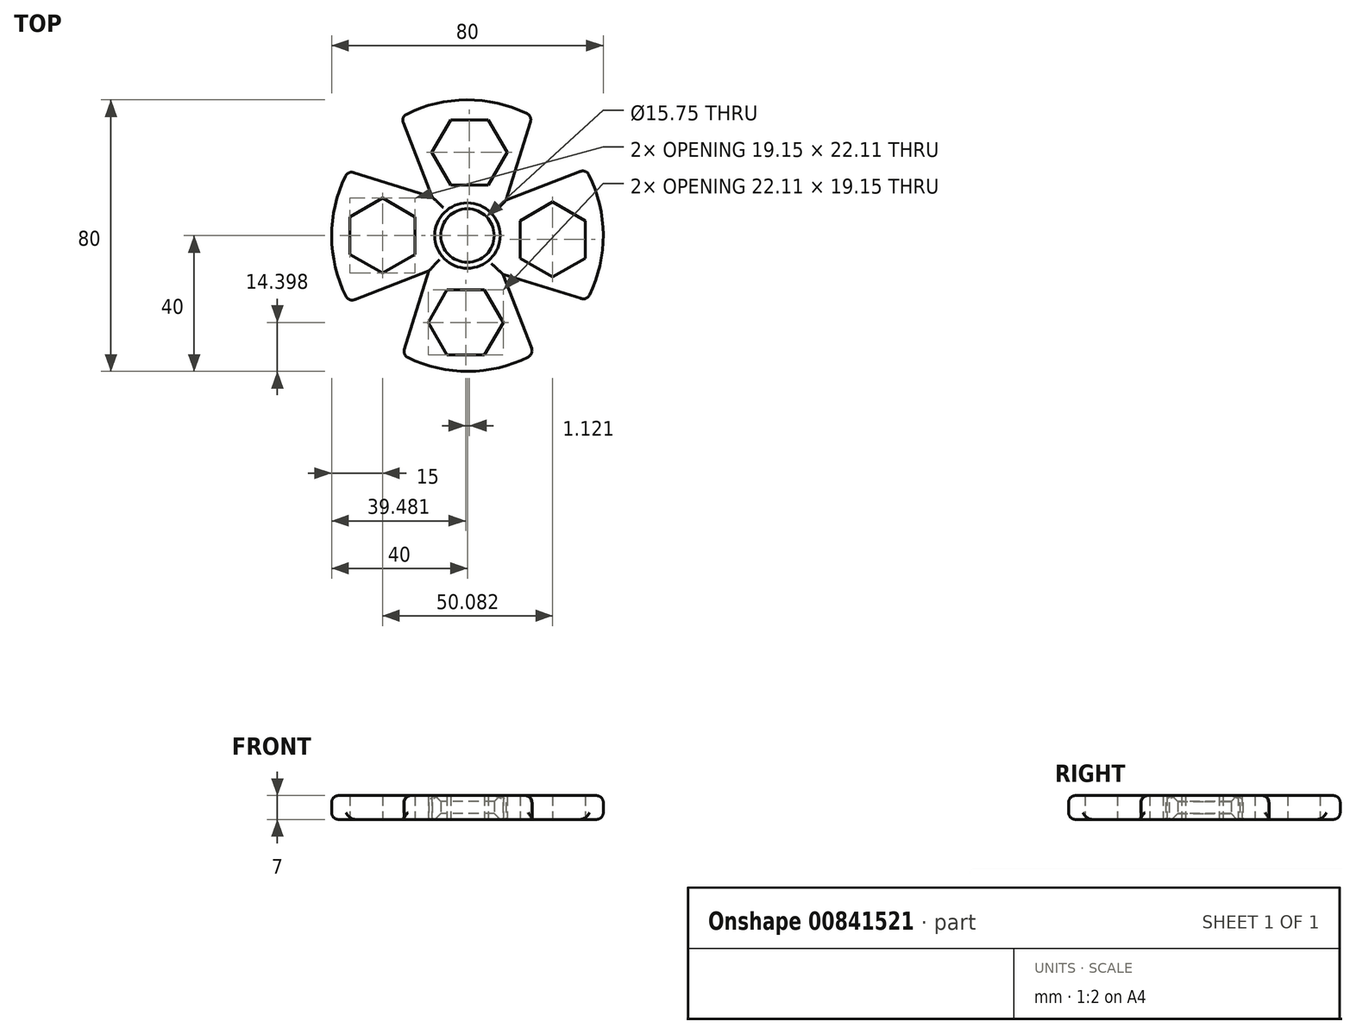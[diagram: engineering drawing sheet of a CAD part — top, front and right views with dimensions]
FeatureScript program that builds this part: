
annotation { "Feature Type Name" : "Feature", "Feature Type Description" : "" }
export const myFeature = defineFeature(function(context is Context, id is Id, definition is map)
    precondition{}
    {
        {
            var Q0;
            Q0=qCreatedBy(makeId("Top.planeOp"),FACE);
            var sketch = newSketch(context, id + "F0", { "sketchPlane" : qUnion([Q0])});
            skCircle(sketch, "E0", {"center": v(0, 0) * mm, "radius": 7.88 * mm});
            skCircle(sketch, "E1", {"center": v(0, 0) * mm, "radius": 40 * mm});
            skSolve(sketch);
        }
        {
            var Q0;
            Q0=makeQuery(id+"F0.imprint","IMPRINT",FACE,{"disambiguationData":[TD([[makeQuery(id+"F0.imprint","IMPRINT",EDGE,{"derivedFrom":sQuery(id+"F0.wireOp",EDGE,"E0")}),-1.0]])]});
            extrude(context, id + "F1", {"entities" : qUnion([Q0]), "depth" : 7 * mm, "offsetDistance" : 25 * mm});
        }
        {
            var Q0;
            Q0=qCreatedBy(makeId("Top.planeOp"),FACE);
            var sketch = newSketch(context, id + "F2", { "sketchPlane" : qUnion([Q0])});
            skCircle(sketch, "E2.cCircle", {"center": v(-25, 0) * mm, "radius": 9.58 * mm, "construction": true});
            skLineSegment(sketch, "E2.0", {"start": v(-15.42, -5.53) * mm, "end": v(-25, -11.06) * mm});
            skLineSegment(sketch, "E2.1", {"start": v(-25, -11.06) * mm, "end": v(-34.57, -5.53) * mm});
            skLineSegment(sketch, "E2.2", {"start": v(-34.57, -5.53) * mm, "end": v(-34.58, 5.53) * mm});
            skLineSegment(sketch, "E2.3", {"start": v(-34.58, 5.53) * mm, "end": v(-25, 11.06) * mm});
            skLineSegment(sketch, "E2.4", {"start": v(-25, 11.06) * mm, "end": v(-15.43, 5.53) * mm});
            skLineSegment(sketch, "E2.5", {"start": v(-15.43, 5.53) * mm, "end": v(-15.42, -5.53) * mm});
            skPoint(sketch, "E2.0.midPoint", {"position": v(-20.21, -8.3) * mm});
            skLineSegment(sketch, "E3.1.0", {"start": v(-11.58, -25.6) * mm, "end": v(-6.05, -16.03) * mm});
            skLineSegment(sketch, "E3.1.1", {"start": v(-6.05, -35.18) * mm, "end": v(-11.58, -25.6) * mm});
            skLineSegment(sketch, "E3.1.2", {"start": v(5, -35.18) * mm, "end": v(-6.05, -35.18) * mm});
            skLineSegment(sketch, "E3.1.3", {"start": v(10.54, -25.6) * mm, "end": v(5, -35.18) * mm});
            skLineSegment(sketch, "E3.1.4", {"start": v(5, -16.03) * mm, "end": v(10.54, -25.6) * mm});
            skLineSegment(sketch, "E3.1.5", {"start": v(-6.05, -16.03) * mm, "end": v(5, -16.03) * mm});
            skLineSegment(sketch, "E3.2.0", {"start": v(25.08, -12.18) * mm, "end": v(15.5, -6.65) * mm});
            skLineSegment(sketch, "E3.2.1", {"start": v(34.66, -6.65) * mm, "end": v(25.08, -12.18) * mm});
            skLineSegment(sketch, "E3.2.2", {"start": v(34.66, 4.4) * mm, "end": v(34.66, -6.65) * mm});
            skLineSegment(sketch, "E3.2.3", {"start": v(25.08, 9.94) * mm, "end": v(34.66, 4.4) * mm});
            skLineSegment(sketch, "E3.2.4", {"start": v(15.5, 4.4) * mm, "end": v(25.08, 9.94) * mm});
            skLineSegment(sketch, "E3.2.5", {"start": v(15.5, -6.65) * mm, "end": v(15.5, 4.4) * mm});
            skLineSegment(sketch, "E3.3.0", {"start": v(11.66, 24.48) * mm, "end": v(6.13, 14.9) * mm});
            skLineSegment(sketch, "E3.3.1", {"start": v(6.13, 34.06) * mm, "end": v(11.66, 24.48) * mm});
            skLineSegment(sketch, "E3.3.2", {"start": v(-4.93, 34.06) * mm, "end": v(6.13, 34.06) * mm});
            skLineSegment(sketch, "E3.3.3", {"start": v(-10.45, 24.48) * mm, "end": v(-4.93, 34.06) * mm});
            skLineSegment(sketch, "E3.3.4", {"start": v(-4.93, 14.9) * mm, "end": v(-10.45, 24.48) * mm});
            skLineSegment(sketch, "E3.3.5", {"start": v(6.13, 14.9) * mm, "end": v(-4.93, 14.9) * mm});
            skPoint(sketch, "E3.center", {"position": v(0.04, -0.56) * mm});
            skSolve(sketch);
        }
        {
            var Q0;
            Q0=qSketchRegion(id+"F2",true);
            extrude(context, id + "F3", {"entities" : qUnion([Q0]), "operationType" : NewBodyOperationType.REMOVE, "endBound" : BoundingType.THROUGH_ALL, "depth" : 25 * mm, "offsetDistance" : 25 * mm});
        }
        {
            var Q0;
            Q0=qCreatedBy(makeId("Top.planeOp"),FACE);
            var sketch = newSketch(context, id + "F4", { "sketchPlane" : qUnion([Q0])});
            skLineSegment(sketch, "E4", {"start": v(-19.58, 35.02) * mm, "end": v(-10.44, 11.39) * mm});
            skLineSegment(sketch, "E5", {"start": v(-10.44, 11.39) * mm, "end": v(-58.22, 26.22) * mm});
            skLineSegment(sketch, "E6", {"start": v(-58.22, 26.22) * mm, "end": v(-19.58, 35.02) * mm});
            skLineSegment(sketch, "E7.1.0", {"start": v(-26.22, -58.22) * mm, "end": v(-35.02, -19.58) * mm});
            skLineSegment(sketch, "E7.1.1", {"start": v(-11.39, -10.44) * mm, "end": v(-26.22, -58.22) * mm});
            skLineSegment(sketch, "E7.1.2", {"start": v(-35.02, -19.58) * mm, "end": v(-11.39, -10.44) * mm});
            skLineSegment(sketch, "E7.2.0", {"start": v(58.22, -26.22) * mm, "end": v(19.58, -35.02) * mm});
            skLineSegment(sketch, "E7.2.1", {"start": v(10.44, -11.39) * mm, "end": v(58.22, -26.22) * mm});
            skLineSegment(sketch, "E7.2.2", {"start": v(19.58, -35.02) * mm, "end": v(10.44, -11.39) * mm});
            skLineSegment(sketch, "E7.3.0", {"start": v(26.22, 58.22) * mm, "end": v(35.02, 19.58) * mm});
            skLineSegment(sketch, "E7.3.1", {"start": v(11.39, 10.44) * mm, "end": v(26.22, 58.22) * mm});
            skLineSegment(sketch, "E7.3.2", {"start": v(35.02, 19.58) * mm, "end": v(11.39, 10.44) * mm});
            skPoint(sketch, "E7.center", {"position": v(0, 0) * mm});
            skSolve(sketch);
        }
        {
            var Q0;
            Q0=makeQuery(id+"F4.imprint","IMPRINT",FACE,{"disambiguationData":[TD([[makeQuery(id+"F4.imprint","IMPRINT",EDGE,{"derivedFrom":sQuery(id+"F4.wireOp",EDGE,"E4")}),-1.0]])]});
            var Q1;
            Q1=makeQuery(id+"F4.imprint","IMPRINT",FACE,{"disambiguationData":[TD([[makeQuery(id+"F4.imprint","IMPRINT",EDGE,{"derivedFrom":sQuery(id+"F4.wireOp",EDGE,"E7.1.0")}),-1.0]])]});
            var Q2;
            Q2=makeQuery(id+"F4.imprint","IMPRINT",FACE,{"disambiguationData":[TD([[makeQuery(id+"F4.imprint","IMPRINT",EDGE,{"derivedFrom":sQuery(id+"F4.wireOp",EDGE,"E7.2.0")}),-1.0]])]});
            var Q3;
            Q3=makeQuery(id+"F4.imprint","IMPRINT",FACE,{"disambiguationData":[TD([[makeQuery(id+"F4.imprint","IMPRINT",EDGE,{"derivedFrom":sQuery(id+"F4.wireOp",EDGE,"E7.3.0")}),-1.0]])]});
            extrude(context, id + "F5", {"entities" : qUnion([Q0, Q1, Q2, Q3]), "operationType" : NewBodyOperationType.REMOVE, "endBound" : BoundingType.THROUGH_ALL, "depth" : 25 * mm, "offsetDistance" : 25 * mm});
        }
        {
            var Q0;
            Q0=makeQuery(id+"F5.boolean.opBoolean","INTERSECT",EDGE,{"derivedFrom":[makeQuery(id+"F1.opExtrude","CAP_FACE",FACE,{"disambiguationData":[OSD([sQuery(id+"F0.wireOp",EDGE,"E0"),sQuery(id+"F0.wireOp",EDGE,"E1")])],"isStart":false}),makeQuery(id+"F5.opExtrude","SWEPT_FACE",FACE,{"disambiguationData":[OSD([sQuery(id+"F4.wireOp",EDGE,"E5")])]})]});
            var Q1;
            {var subQ0=sQuery(id+"F0.wireOp",EDGE,"E1");Q1=makeQuery(id+"F5.boolean.opBoolean","SPLIT",EDGE,{"disambiguationData":[TD([makeQuery(id+"F5.opExtrude","SWEPT_FACE",FACE,{"disambiguationData":[OSD([sQuery(id+"F4.wireOp",EDGE,"E5")])]})])],"derivedFrom":makeQuery(id+"F1.opExtrude","CAP_EDGE",EDGE,{"disambiguationData":[OSD([subQ0])],"isStart":false})});}
            var Q2;
            Q2=makeQuery(id+"F5.boolean.opBoolean","INTERSECT",EDGE,{"derivedFrom":[makeQuery(id+"F1.opExtrude","CAP_FACE",FACE,{"disambiguationData":[OSD([sQuery(id+"F0.wireOp",EDGE,"E0"),sQuery(id+"F0.wireOp",EDGE,"E1")])],"isStart":false}),makeQuery(id+"F5.opExtrude","SWEPT_FACE",FACE,{"disambiguationData":[OSD([sQuery(id+"F4.wireOp",EDGE,"E7.1.2")])]})]});
            var Q3;
            Q3=makeQuery(id+"F5.boolean.opBoolean","INTERSECT",EDGE,{"derivedFrom":[makeQuery(id+"F1.opExtrude","CAP_FACE",FACE,{"disambiguationData":[OSD([sQuery(id+"F0.wireOp",EDGE,"E0"),sQuery(id+"F0.wireOp",EDGE,"E1")])],"isStart":false}),makeQuery(id+"F5.opExtrude","SWEPT_FACE",FACE,{"disambiguationData":[OSD([sQuery(id+"F4.wireOp",EDGE,"E7.1.1")])]})]});
            var Q4;
            Q4=makeQuery(id+"F5.boolean.opBoolean","INTERSECT",EDGE,{"derivedFrom":[makeQuery(id+"F1.opExtrude","CAP_FACE",FACE,{"disambiguationData":[OSD([sQuery(id+"F0.wireOp",EDGE,"E0"),sQuery(id+"F0.wireOp",EDGE,"E1")])],"isStart":false}),makeQuery(id+"F5.opExtrude","SWEPT_FACE",FACE,{"disambiguationData":[OSD([sQuery(id+"F4.wireOp",EDGE,"E7.2.2")])]})]});
            var Q5;
            Q5=makeQuery(id+"F5.boolean.opBoolean","INTERSECT",EDGE,{"derivedFrom":[makeQuery(id+"F1.opExtrude","CAP_FACE",FACE,{"disambiguationData":[OSD([sQuery(id+"F0.wireOp",EDGE,"E0"),sQuery(id+"F0.wireOp",EDGE,"E1")])],"isStart":false}),makeQuery(id+"F5.opExtrude","SWEPT_FACE",FACE,{"disambiguationData":[OSD([sQuery(id+"F4.wireOp",EDGE,"E7.2.1")])]})]});
            var Q6;
            Q6=makeQuery(id+"F5.boolean.opBoolean","INTERSECT",EDGE,{"derivedFrom":[makeQuery(id+"F1.opExtrude","CAP_FACE",FACE,{"disambiguationData":[OSD([sQuery(id+"F0.wireOp",EDGE,"E0"),sQuery(id+"F0.wireOp",EDGE,"E1")])],"isStart":false}),makeQuery(id+"F5.opExtrude","SWEPT_FACE",FACE,{"disambiguationData":[OSD([sQuery(id+"F4.wireOp",EDGE,"E7.3.2")])]})]});
            var Q7;
            {var subQ0=sQuery(id+"F0.wireOp",EDGE,"E1");Q7=makeQuery(id+"F5.boolean.opBoolean","SPLIT",EDGE,{"disambiguationData":[TD([makeQuery(id+"F5.opExtrude","SWEPT_FACE",FACE,{"disambiguationData":[OSD([sQuery(id+"F4.wireOp",EDGE,"E7.2.1")])]})])],"derivedFrom":makeQuery(id+"F1.opExtrude","CAP_EDGE",EDGE,{"disambiguationData":[OSD([subQ0])],"isStart":false})});}
            var Q8;
            Q8=makeQuery(id+"F5.boolean.opBoolean","INTERSECT",EDGE,{"derivedFrom":[makeQuery(id+"F1.opExtrude","CAP_FACE",FACE,{"disambiguationData":[OSD([sQuery(id+"F0.wireOp",EDGE,"E0"),sQuery(id+"F0.wireOp",EDGE,"E1")])],"isStart":false}),makeQuery(id+"F5.opExtrude","SWEPT_FACE",FACE,{"disambiguationData":[OSD([sQuery(id+"F4.wireOp",EDGE,"E7.3.1")])]})]});
            var Q9;
            {var subQ0=sQuery(id+"F0.wireOp",EDGE,"E1");Q9=makeQuery(id+"F5.boolean.opBoolean","SPLIT",EDGE,{"disambiguationData":[TD([makeQuery(id+"F5.opExtrude","SWEPT_FACE",FACE,{"disambiguationData":[OSD([sQuery(id+"F4.wireOp",EDGE,"E4")])]})])],"derivedFrom":makeQuery(id+"F1.opExtrude","CAP_EDGE",EDGE,{"disambiguationData":[OSD([subQ0])],"isStart":false})});}
            var Q10;
            Q10=makeQuery(id+"F5.boolean.opBoolean","INTERSECT",EDGE,{"derivedFrom":[makeQuery(id+"F1.opExtrude","CAP_FACE",FACE,{"disambiguationData":[OSD([sQuery(id+"F0.wireOp",EDGE,"E0"),sQuery(id+"F0.wireOp",EDGE,"E1")])],"isStart":false}),makeQuery(id+"F5.opExtrude","SWEPT_FACE",FACE,{"disambiguationData":[OSD([sQuery(id+"F4.wireOp",EDGE,"E4")])]})]});
            var Q11;
            {var subQ0=sQuery(id+"F0.wireOp",EDGE,"E1");Q11=makeQuery(id+"F5.boolean.opBoolean","SPLIT",EDGE,{"disambiguationData":[TD([makeQuery(id+"F5.opExtrude","SWEPT_FACE",FACE,{"disambiguationData":[OSD([sQuery(id+"F4.wireOp",EDGE,"E5")])]})])],"derivedFrom":makeQuery(id+"F1.opExtrude","CAP_EDGE",EDGE,{"disambiguationData":[OSD([subQ0])],"isStart":true})});}
            var Q12;
            Q12=makeQuery(id+"F5.boolean.opBoolean","COPY",EDGE,{"derivedFrom":makeQuery(id+"F5.opExtrude","CAP_EDGE",EDGE,{"disambiguationData":[OSD([sQuery(id+"F4.wireOp",EDGE,"E5")])],"isStart":true})});
            var Q13;
            Q13=makeQuery(id+"F5.boolean.opBoolean","COPY",EDGE,{"derivedFrom":makeQuery(id+"F5.opExtrude","CAP_EDGE",EDGE,{"disambiguationData":[OSD([sQuery(id+"F4.wireOp",EDGE,"E4")])],"isStart":true})});
            var Q14;
            {var subQ0=sQuery(id+"F0.wireOp",EDGE,"E1");Q14=makeQuery(id+"F5.boolean.opBoolean","SPLIT",EDGE,{"disambiguationData":[TD([makeQuery(id+"F5.opExtrude","SWEPT_FACE",FACE,{"disambiguationData":[OSD([sQuery(id+"F4.wireOp",EDGE,"E4")])]})])],"derivedFrom":makeQuery(id+"F1.opExtrude","CAP_EDGE",EDGE,{"disambiguationData":[OSD([subQ0])],"isStart":true})});}
            var Q15;
            Q15=makeQuery(id+"F5.boolean.opBoolean","COPY",EDGE,{"derivedFrom":makeQuery(id+"F5.opExtrude","CAP_EDGE",EDGE,{"disambiguationData":[OSD([sQuery(id+"F4.wireOp",EDGE,"E7.3.1")])],"isStart":true})});
            var Q16;
            Q16=makeQuery(id+"F5.boolean.opBoolean","COPY",EDGE,{"derivedFrom":makeQuery(id+"F5.opExtrude","CAP_EDGE",EDGE,{"disambiguationData":[OSD([sQuery(id+"F4.wireOp",EDGE,"E7.3.2")])],"isStart":true})});
            var Q17;
            {var subQ0=sQuery(id+"F0.wireOp",EDGE,"E1");Q17=makeQuery(id+"F5.boolean.opBoolean","SPLIT",EDGE,{"disambiguationData":[TD([makeQuery(id+"F5.opExtrude","SWEPT_FACE",FACE,{"disambiguationData":[OSD([sQuery(id+"F4.wireOp",EDGE,"E7.2.1")])]})])],"derivedFrom":makeQuery(id+"F1.opExtrude","CAP_EDGE",EDGE,{"disambiguationData":[OSD([subQ0])],"isStart":true})});}
            var Q18;
            Q18=makeQuery(id+"F5.boolean.opBoolean","COPY",EDGE,{"derivedFrom":makeQuery(id+"F5.opExtrude","CAP_EDGE",EDGE,{"disambiguationData":[OSD([sQuery(id+"F4.wireOp",EDGE,"E7.2.1")])],"isStart":true})});
            var Q19;
            Q19=makeQuery(id+"F5.boolean.opBoolean","COPY",EDGE,{"derivedFrom":makeQuery(id+"F5.opExtrude","CAP_EDGE",EDGE,{"disambiguationData":[OSD([sQuery(id+"F4.wireOp",EDGE,"E7.2.2")])],"isStart":true})});
            var Q20;
            {var subQ0=sQuery(id+"F0.wireOp",EDGE,"E1");Q20=makeQuery(id+"F5.boolean.opBoolean","SPLIT",EDGE,{"disambiguationData":[TD([makeQuery(id+"F5.opExtrude","SWEPT_FACE",FACE,{"disambiguationData":[OSD([sQuery(id+"F4.wireOp",EDGE,"E7.1.1")])]})])],"derivedFrom":makeQuery(id+"F1.opExtrude","CAP_EDGE",EDGE,{"disambiguationData":[OSD([subQ0])],"isStart":true})});}
            var Q21;
            Q21=makeQuery(id+"F5.boolean.opBoolean","COPY",EDGE,{"derivedFrom":makeQuery(id+"F5.opExtrude","CAP_EDGE",EDGE,{"disambiguationData":[OSD([sQuery(id+"F4.wireOp",EDGE,"E7.1.1")])],"isStart":true})});
            var Q22;
            Q22=makeQuery(id+"F5.boolean.opBoolean","COPY",EDGE,{"derivedFrom":makeQuery(id+"F5.opExtrude","CAP_EDGE",EDGE,{"disambiguationData":[OSD([sQuery(id+"F4.wireOp",EDGE,"E7.1.2")])],"isStart":true})});
            var Q23;
            {var subQ0=sQuery(id+"F0.wireOp",EDGE,"E1");Q23=makeQuery(id+"F5.boolean.opBoolean","SPLIT",EDGE,{"disambiguationData":[TD([makeQuery(id+"F5.opExtrude","SWEPT_FACE",FACE,{"disambiguationData":[OSD([sQuery(id+"F4.wireOp",EDGE,"E7.1.1")])]})])],"derivedFrom":makeQuery(id+"F1.opExtrude","CAP_EDGE",EDGE,{"disambiguationData":[OSD([subQ0])],"isStart":false})});}
            var Q24;
            Q24=makeQuery(id+"F5.boolean.opBoolean","INTERSECT",EDGE,{"derivedFrom":[makeQuery(id+"F1.opExtrude","SWEPT_FACE",FACE,{"disambiguationData":[OSD([sQuery(id+"F0.wireOp",EDGE,"E1")])]}),makeQuery(id+"F5.opExtrude","SWEPT_FACE",FACE,{"disambiguationData":[OSD([sQuery(id+"F4.wireOp",EDGE,"E7.2.2")])]})]});
            var Q25;
            Q25=makeQuery(id+"F5.boolean.opBoolean","INTERSECT",EDGE,{"derivedFrom":[makeQuery(id+"F1.opExtrude","SWEPT_FACE",FACE,{"disambiguationData":[OSD([sQuery(id+"F0.wireOp",EDGE,"E1")])]}),makeQuery(id+"F5.opExtrude","SWEPT_FACE",FACE,{"disambiguationData":[OSD([sQuery(id+"F4.wireOp",EDGE,"E7.1.1")])]})]});
            var Q26;
            Q26=makeQuery(id+"F5.boolean.opBoolean","INTERSECT",EDGE,{"derivedFrom":[makeQuery(id+"F1.opExtrude","SWEPT_FACE",FACE,{"disambiguationData":[OSD([sQuery(id+"F0.wireOp",EDGE,"E1")])]}),makeQuery(id+"F5.opExtrude","SWEPT_FACE",FACE,{"disambiguationData":[OSD([sQuery(id+"F4.wireOp",EDGE,"E7.1.2")])]})]});
            var Q27;
            Q27=makeQuery(id+"F5.boolean.opBoolean","INTERSECT",EDGE,{"derivedFrom":[makeQuery(id+"F1.opExtrude","SWEPT_FACE",FACE,{"disambiguationData":[OSD([sQuery(id+"F0.wireOp",EDGE,"E1")])]}),makeQuery(id+"F5.opExtrude","SWEPT_FACE",FACE,{"disambiguationData":[OSD([sQuery(id+"F4.wireOp",EDGE,"E5")])]})]});
            var Q28;
            Q28=makeQuery(id+"F5.boolean.opBoolean","INTERSECT",EDGE,{"derivedFrom":[makeQuery(id+"F1.opExtrude","SWEPT_FACE",FACE,{"disambiguationData":[OSD([sQuery(id+"F0.wireOp",EDGE,"E1")])]}),makeQuery(id+"F5.opExtrude","SWEPT_FACE",FACE,{"disambiguationData":[OSD([sQuery(id+"F4.wireOp",EDGE,"E4")])]})]});
            var Q29;
            Q29=makeQuery(id+"F5.boolean.opBoolean","INTERSECT",EDGE,{"derivedFrom":[makeQuery(id+"F1.opExtrude","SWEPT_FACE",FACE,{"disambiguationData":[OSD([sQuery(id+"F0.wireOp",EDGE,"E1")])]}),makeQuery(id+"F5.opExtrude","SWEPT_FACE",FACE,{"disambiguationData":[OSD([sQuery(id+"F4.wireOp",EDGE,"E7.3.1")])]})]});
            var Q30;
            Q30=makeQuery(id+"F5.boolean.opBoolean","INTERSECT",EDGE,{"derivedFrom":[makeQuery(id+"F1.opExtrude","SWEPT_FACE",FACE,{"disambiguationData":[OSD([sQuery(id+"F0.wireOp",EDGE,"E1")])]}),makeQuery(id+"F5.opExtrude","SWEPT_FACE",FACE,{"disambiguationData":[OSD([sQuery(id+"F4.wireOp",EDGE,"E7.3.2")])]})]});
            var Q31;
            Q31=makeQuery(id+"F5.boolean.opBoolean","INTERSECT",EDGE,{"derivedFrom":[makeQuery(id+"F1.opExtrude","SWEPT_FACE",FACE,{"disambiguationData":[OSD([sQuery(id+"F0.wireOp",EDGE,"E1")])]}),makeQuery(id+"F5.opExtrude","SWEPT_FACE",FACE,{"disambiguationData":[OSD([sQuery(id+"F4.wireOp",EDGE,"E7.2.1")])]})]});
            fillet(context, id + "F6", {"entities" : qUnion([Q0, Q1, Q2, Q3, Q4, Q5, Q6, Q7, Q8, Q9, Q10, Q11, Q12, Q13, Q14, Q15, Q16, Q17, Q18, Q19, Q20, Q21, Q22, Q23, Q24, Q25, Q26, Q27, Q28, Q29, Q30, Q31]), "radius" : 2 * mm, "tangentPropagation" : true, "allowEdgeOverflow" : false});
        }
        {
            var Q0;
            Q0=makeQuery(id+"F1.opExtrude","CAP_EDGE",EDGE,{"disambiguationData":[OSD([sQuery(id+"F0.wireOp",EDGE,"E0")])],"isStart":false});
            var Q1;
            Q1=makeQuery(id+"F1.opExtrude","CAP_EDGE",EDGE,{"disambiguationData":[OSD([sQuery(id+"F0.wireOp",EDGE,"E0")])],"isStart":true});
            chamfer(context, id + "F7", {"entities" : qUnion([Q0, Q1]), "width" : 1.75 * mm, "tangentPropagation" : true});
        }
    });
